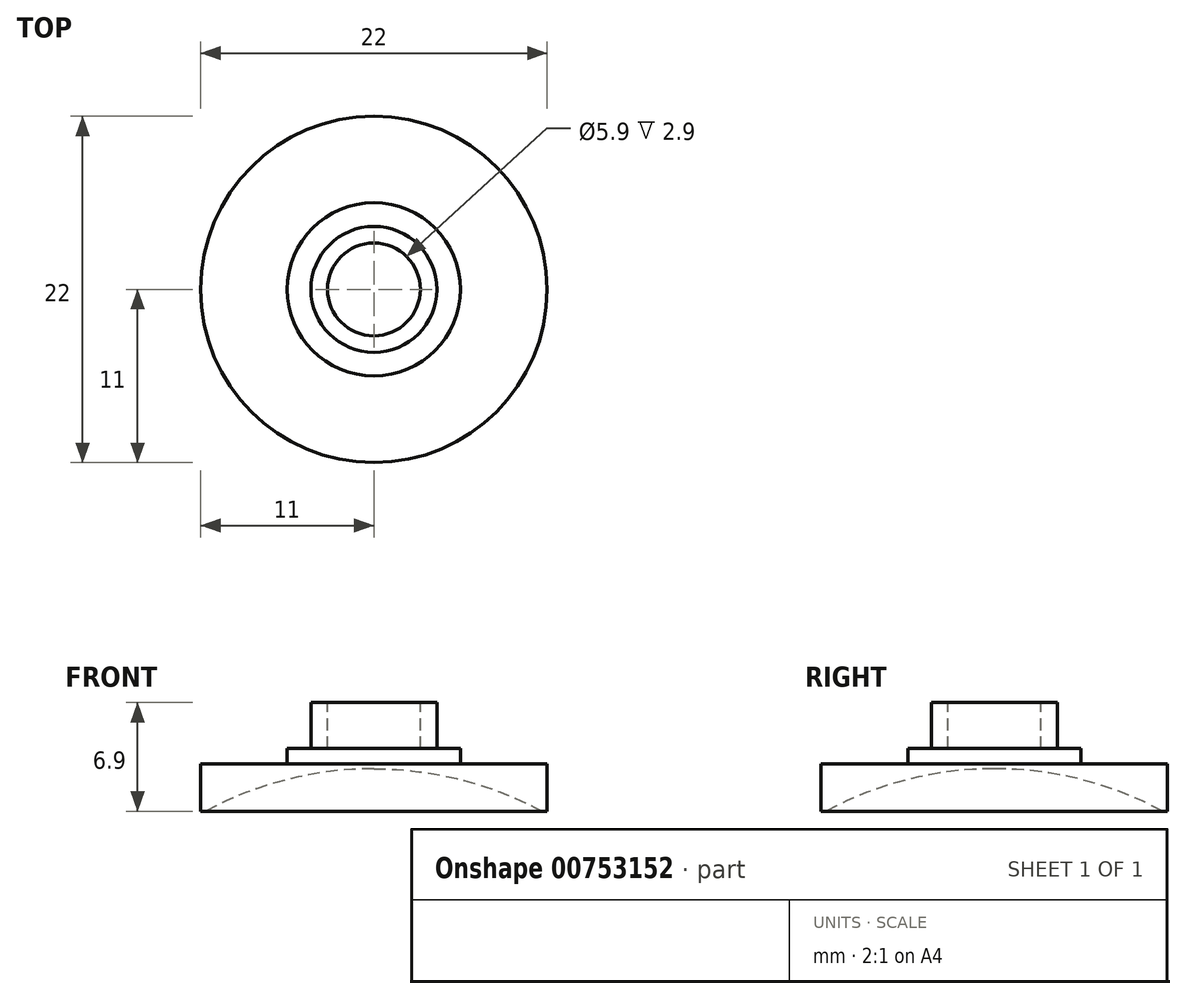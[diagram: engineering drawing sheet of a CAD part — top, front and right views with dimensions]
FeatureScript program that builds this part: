
annotation { "Feature Type Name" : "Feature", "Feature Type Description" : "" }
export const myFeature = defineFeature(function(context is Context, id is Id, definition is map)
    precondition{}
    {
        {
            var Q0;
            Q0=qCreatedBy(makeId("Top.planeOp"),FACE);
            var sketch = newSketch(context, id + "F0", { "sketchPlane" : qUnion([Q0])});
            skCircle(sketch, "E0", {"center": v(0, 0) * mm, "radius": 11 * mm});
            skSolve(sketch);
        }
        {
            var Q0;
            Q0=qSketchRegion(id+"F0",true);
            extrude(context, id + "F1", {"entities" : qUnion([Q0]), "depth" : 3 * mm, "offsetDistance" : 25 * mm});
        }
        {
            var Q0;
            Q0=qCreatedBy(makeId("Front.planeOp"),FACE);
            var sketch = newSketch(context, id + "F2", { "sketchPlane" : qUnion([Q0])});
            skLineSegment(sketch, "E1", {"start": v(0, 0) * mm, "end": v(0, -4.5) * mm, "construction": true});
            skSolve(sketch);
        }
        {
            var Q0;
            Q0=qCreatedBy(makeId("Front.planeOp"),FACE);
            var sketch = newSketch(context, id + "F3", { "sketchPlane" : qUnion([Q0])});
            skArc(sketch, "E2", {"start": v(0, 2.7) * mm, "mid": v(-22.55, -19.85) * mm, "end": v(0, -42.4) * mm});
            skLineSegment(sketch, "E3", {"start": v(0, 2.7) * mm, "end": v(0, -42.4) * mm});
            skPoint(sketch, "E4", {"position": v(-10.7, 0) * mm});
            skSolve(sketch);
        }
        {
            var Q0;
            Q0=qSketchRegion(id+"F3",true);
            var Q1;
            Q1=sQuery(id+"F3.wireOp",EDGE,"E3");
            revolve(context, id + "F4", {"operationType" : NewBodyOperationType.REMOVE, "surfaceOperationType" : NewSurfaceOperationType.NEW, "entities" : qUnion([Q0]), "axis" : qUnion([Q1]), "revolveType" : RevolveType.FULL, "oppositeDirection" : true});
        }
        {
            var Q0;
            Q0=makeQuery(id+"F1.opExtrude","CAP_FACE",FACE,{"disambiguationData":[OSD([sQuery(id+"F0.wireOp",EDGE,"E0")])],"isStart":false});
            var sketch = newSketch(context, id + "F5", { "sketchPlane" : qUnion([Q0])});
            skCircle(sketch, "E5", {"center": v(0, 0) * mm, "radius": 5.5 * mm});
            skSolve(sketch);
        }
        {
            var Q0;
            Q0=qSketchRegion(id+"F5",true);
            extrude(context, id + "F6", {"entities" : qUnion([Q0]), "operationType" : NewBodyOperationType.ADD, "depth" : 1 * mm, "offsetDistance" : 25 * mm});
        }
        {
            var Q0;
            Q0=makeQuery(id+"F6.opExtrude","CAP_FACE",FACE,{"disambiguationData":[OSD([sQuery(id+"F5.wireOp",EDGE,"E5")])],"isStart":false});
            var sketch = newSketch(context, id + "F7", { "sketchPlane" : qUnion([Q0])});
            skCircle(sketch, "E6", {"center": v(0, 0) * mm, "radius": 4 * mm});
            skSolve(sketch);
        }
        {
            var Q0;
            Q0=qSketchRegion(id+"F7",true);
            extrude(context, id + "F8", {"entities" : qUnion([Q0]), "operationType" : NewBodyOperationType.ADD, "depth" : 2.9 * mm, "offsetDistance" : 25 * mm});
        }
        {
            var Q0;
            Q0=makeQuery(id+"F8.opExtrude","CAP_FACE",FACE,{"disambiguationData":[OSD([sQuery(id+"F7.wireOp",EDGE,"E6")])],"isStart":false});
            var sketch = newSketch(context, id + "F9", { "sketchPlane" : qUnion([Q0])});
            skCircle(sketch, "E7", {"center": v(0, 0) * mm, "radius": 2.95 * mm});
            skSolve(sketch);
        }
        {
            var Q0;
            Q0=qSketchRegion(id+"F9",true);
            extrude(context, id + "F10", {"entities" : qUnion([Q0]), "operationType" : NewBodyOperationType.REMOVE, "oppositeDirection" : true, "depth" : 2.9 * mm, "offsetDistance" : 25 * mm});
        }
        {
            var Q0;
            Q0=makeQuery(id+"F4.boolean.opBoolean","INTERSECT",EDGE,{"derivedFrom":[makeQuery(id+"F1.opExtrude","CAP_FACE",FACE,{"disambiguationData":[OSD([sQuery(id+"F0.wireOp",EDGE,"E0")])],"isStart":true}),makeQuery(id+"F4.opRevolve","SWEPT_FACE",FACE,{"disambiguationData":[OSD([sQuery(id+"F3.wireOp",EDGE,"E2")])]})]});
            fillet(context, id + "F11", {"entities" : qUnion([Q0]), "radius" : 0.3 * mm, "tangentPropagation" : true, "allowEdgeOverflow" : false});
        }
    });
